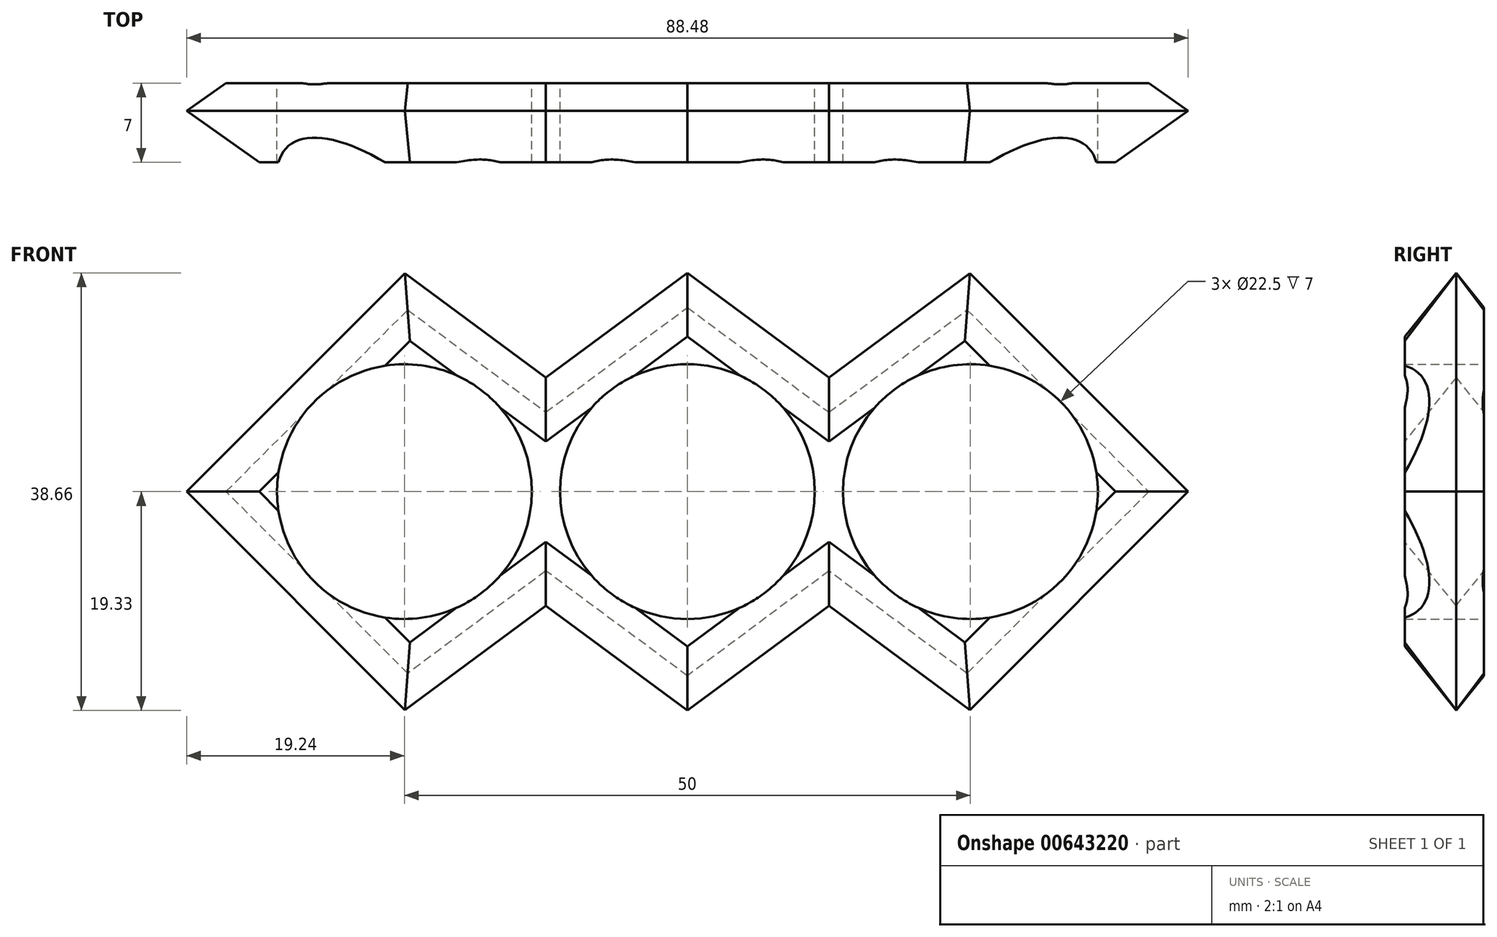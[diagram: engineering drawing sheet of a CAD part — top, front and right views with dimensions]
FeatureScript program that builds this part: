
annotation { "Feature Type Name" : "Feature", "Feature Type Description" : "" }
export const myFeature = defineFeature(function(context is Context, id is Id, definition is map)
    precondition{}
    {
        {
            var Q0;
            Q0=qCreatedBy(makeId("Front.planeOp"),FACE);
            var sketch = newSketch(context, id + "F0", { "sketchPlane" : qUnion([Q0])});
            skCircle(sketch, "E0", {"center": v(0, 0) * mm, "radius": 11.25 * mm});
            skLineSegment(sketch, "E1", {"start": v(0, 0) * mm, "end": v(-25, 0) * mm});
            skLineSegment(sketch, "E2.MirrorCS", {"start": v(0, 0) * mm, "end": v(25, 0) * mm});
            skCircle(sketch, "E3", {"center": v(-25, 0) * mm, "radius": 11.25 * mm});
            skCircle(sketch, "E4", {"center": v(25, 0) * mm, "radius": 11.25 * mm});
            skLineSegment(sketch, "E5", {"start": v(-25, 0) * mm, "end": v(-45, 0) * mm});
            skLineSegment(sketch, "E6.MirrorCS", {"start": v(25, 0) * mm, "end": v(45, 0) * mm});
            skLineSegment(sketch, "E7", {"start": v(-25, 0) * mm, "end": v(-25, 20) * mm});
            skLineSegment(sketch, "E8", {"start": v(-25, 0) * mm, "end": v(-25, -20) * mm});
            skLineSegment(sketch, "E9", {"start": v(-12.5, 0) * mm, "end": v(-12.5, 10.75) * mm});
            skLineSegment(sketch, "E10.MirrorCS", {"start": v(-12.5, 0) * mm, "end": v(-12.5, -10.75) * mm});
            skLineSegment(sketch, "E11", {"start": v(0, 0) * mm, "end": v(0, 20) * mm});
            skLineSegment(sketch, "E12", {"start": v(0, 0) * mm, "end": v(0, -20) * mm});
            skLineSegment(sketch, "E13.MirrorCS", {"start": v(12.5, 0) * mm, "end": v(12.5, 10.75) * mm});
            skLineSegment(sketch, "E14.MirrorCS", {"start": v(12.5, 0) * mm, "end": v(12.5, -10.75) * mm});
            skLineSegment(sketch, "E15", {"start": v(-45, 0) * mm, "end": v(-25, -20) * mm});
            skLineSegment(sketch, "E16", {"start": v(-25, -20) * mm, "end": v(-12.5, -10.75) * mm});
            skLineSegment(sketch, "E17", {"start": v(-12.5, -10.75) * mm, "end": v(0, -20) * mm});
            skLineSegment(sketch, "E18", {"start": v(0, -20) * mm, "end": v(12.5, -10.75) * mm});
            skLineSegment(sketch, "E19", {"start": v(-12.5, 10.75) * mm, "end": v(-25, 20) * mm});
            skLineSegment(sketch, "E20", {"start": v(-25, 20) * mm, "end": v(-45, 0) * mm});
            skLineSegment(sketch, "E21", {"start": v(-12.5, 10.75) * mm, "end": v(0, 20) * mm});
            skLineSegment(sketch, "E22.MirrorCS", {"start": v(12.5, 10.75) * mm, "end": v(0, 20) * mm});
            skLineSegment(sketch, "E23.MirrorCS", {"start": v(12.5, 10.75) * mm, "end": v(25, 20) * mm});
            skLineSegment(sketch, "E24.MirrorCS", {"start": v(25, 20) * mm, "end": v(45, 0) * mm});
            skLineSegment(sketch, "E25.MirrorCS", {"start": v(45, 0) * mm, "end": v(25, -20) * mm});
            skLineSegment(sketch, "E26.MirrorCS", {"start": v(25, -20) * mm, "end": v(12.5, -10.75) * mm});
            skSolve(sketch);
        }
        {
            var Q0;
            {var subQ5=sQuery(id+"F0.wireOp",EDGE,"E20");Q0=makeQuery(id+"F0.imprint","IMPRINT",FACE,{"disambiguationData":[TD([[makeQuery(id+"F0.imprint","IMPRINT",EDGE,{"derivedFrom":subQ5}),1.0]])]});}
            var Q1;
            {var subQ6=sQuery(id+"F0.wireOp",EDGE,"E9");Q1=makeQuery(id+"F0.imprint","IMPRINT",FACE,{"disambiguationData":[TD([[makeQuery(id+"F0.imprint","IMPRINT",EDGE,{"derivedFrom":subQ6}),1.0]])]});}
            var Q2;
            {var subQ0=sQuery(id+"F0.wireOp",EDGE,"E10.MirrorCS");Q2=makeQuery(id+"F0.imprint","IMPRINT",FACE,{"disambiguationData":[TD([[makeQuery(id+"F0.imprint","IMPRINT",EDGE,{"derivedFrom":subQ0}),-1.0]])]});}
            var Q3;
            {var subQ5=sQuery(id+"F0.wireOp",EDGE,"E15");Q3=makeQuery(id+"F0.imprint","IMPRINT",FACE,{"disambiguationData":[TD([[makeQuery(id+"F0.imprint","IMPRINT",EDGE,{"derivedFrom":subQ5}),1.0]])]});}
            var Q4;
            {var subQ4=sQuery(id+"F0.wireOp",EDGE,"E10.MirrorCS");Q4=makeQuery(id+"F0.imprint","IMPRINT",FACE,{"disambiguationData":[TD([[makeQuery(id+"F0.imprint","IMPRINT",EDGE,{"derivedFrom":subQ4}),1.0]])]});}
            var Q5;
            {var subQ4=sQuery(id+"F0.wireOp",EDGE,"E14.MirrorCS");Q5=makeQuery(id+"F0.imprint","IMPRINT",FACE,{"disambiguationData":[TD([[makeQuery(id+"F0.imprint","IMPRINT",EDGE,{"derivedFrom":subQ4}),-1.0]])]});}
            var Q6;
            {var subQ0=sQuery(id+"F0.wireOp",EDGE,"E13.MirrorCS");Q6=makeQuery(id+"F0.imprint","IMPRINT",FACE,{"disambiguationData":[TD([[makeQuery(id+"F0.imprint","IMPRINT",EDGE,{"derivedFrom":subQ0}),1.0]])]});}
            var Q7;
            {var subQ4=sQuery(id+"F0.wireOp",EDGE,"E9");Q7=makeQuery(id+"F0.imprint","IMPRINT",FACE,{"disambiguationData":[TD([[makeQuery(id+"F0.imprint","IMPRINT",EDGE,{"derivedFrom":subQ4}),-1.0]])]});}
            var Q8;
            {var subQ0=sQuery(id+"F0.wireOp",EDGE,"E13.MirrorCS");Q8=makeQuery(id+"F0.imprint","IMPRINT",FACE,{"disambiguationData":[TD([[makeQuery(id+"F0.imprint","IMPRINT",EDGE,{"derivedFrom":subQ0}),-1.0]])]});}
            var Q9;
            {var subQ0=sQuery(id+"F0.wireOp",EDGE,"E14.MirrorCS");Q9=makeQuery(id+"F0.imprint","IMPRINT",FACE,{"disambiguationData":[TD([[makeQuery(id+"F0.imprint","IMPRINT",EDGE,{"derivedFrom":subQ0}),1.0]])]});}
            extrude(context, id + "F1", {"entities" : qUnion([Q0, Q1, Q2, Q3, Q4, Q5, Q6, Q7, Q8, Q9]), "depth" : 7 * mm, "offsetDistance" : 25.4 * mm});
        }
        {
            var Q0;
            Q0=makeQuery(id+"F1.opExtrude","CAP_EDGE",EDGE,{"disambiguationData":[OSD([sQuery(id+"F0.wireOp",EDGE,"E20")])],"isStart":false});
            var Q1;
            Q1=makeQuery(id+"F1.opExtrude","CAP_EDGE",EDGE,{"disambiguationData":[OSD([sQuery(id+"F0.wireOp",EDGE,"E19")])],"isStart":false});
            var Q2;
            Q2=makeQuery(id+"F1.opExtrude","CAP_EDGE",EDGE,{"disambiguationData":[OSD([sQuery(id+"F0.wireOp",EDGE,"E21")])],"isStart":false});
            var Q3;
            Q3=makeQuery(id+"F1.opExtrude","CAP_EDGE",EDGE,{"disambiguationData":[OSD([sQuery(id+"F0.wireOp",EDGE,"E22.MirrorCS")])],"isStart":false});
            var Q4;
            Q4=makeQuery(id+"F1.opExtrude","CAP_EDGE",EDGE,{"disambiguationData":[OSD([sQuery(id+"F0.wireOp",EDGE,"E23.MirrorCS")])],"isStart":false});
            var Q5;
            Q5=makeQuery(id+"F1.opExtrude","CAP_EDGE",EDGE,{"disambiguationData":[OSD([sQuery(id+"F0.wireOp",EDGE,"E24.MirrorCS")])],"isStart":false});
            var Q6;
            Q6=makeQuery(id+"F1.opExtrude","CAP_EDGE",EDGE,{"disambiguationData":[OSD([sQuery(id+"F0.wireOp",EDGE,"E25.MirrorCS")])],"isStart":false});
            var Q7;
            Q7=makeQuery(id+"F1.opExtrude","CAP_EDGE",EDGE,{"disambiguationData":[OSD([sQuery(id+"F0.wireOp",EDGE,"E26.MirrorCS")])],"isStart":false});
            var Q8;
            Q8=makeQuery(id+"F1.opExtrude","CAP_EDGE",EDGE,{"disambiguationData":[OSD([sQuery(id+"F0.wireOp",EDGE,"E18")])],"isStart":false});
            var Q9;
            Q9=makeQuery(id+"F1.opExtrude","CAP_EDGE",EDGE,{"disambiguationData":[OSD([sQuery(id+"F0.wireOp",EDGE,"E17")])],"isStart":false});
            var Q10;
            Q10=makeQuery(id+"F1.opExtrude","CAP_EDGE",EDGE,{"disambiguationData":[OSD([sQuery(id+"F0.wireOp",EDGE,"E16")])],"isStart":false});
            var Q11;
            Q11=makeQuery(id+"F1.opExtrude","CAP_EDGE",EDGE,{"disambiguationData":[OSD([sQuery(id+"F0.wireOp",EDGE,"E15")])],"isStart":false});
            chamfer(context, id + "F2", {"entities" : qUnion([Q0, Q1, Q2, Q3, Q4, Q5, Q6, Q7, Q8, Q9, Q10, Q11]), "width" : 5.08 * mm, "tangentPropagation" : true});
        }
        {
            var Q0;
            Q0=makeQuery(id+"F1.opExtrude","CAP_EDGE",EDGE,{"disambiguationData":[OSD([sQuery(id+"F0.wireOp",EDGE,"E26.MirrorCS")])],"isStart":true});
            var Q1;
            Q1=makeQuery(id+"F1.opExtrude","CAP_EDGE",EDGE,{"disambiguationData":[OSD([sQuery(id+"F0.wireOp",EDGE,"E25.MirrorCS")])],"isStart":true});
            var Q2;
            Q2=makeQuery(id+"F1.opExtrude","CAP_EDGE",EDGE,{"disambiguationData":[OSD([sQuery(id+"F0.wireOp",EDGE,"E18")])],"isStart":true});
            var Q3;
            Q3=makeQuery(id+"F1.opExtrude","CAP_EDGE",EDGE,{"disambiguationData":[OSD([sQuery(id+"F0.wireOp",EDGE,"E17")])],"isStart":true});
            var Q4;
            Q4=makeQuery(id+"F1.opExtrude","CAP_EDGE",EDGE,{"disambiguationData":[OSD([sQuery(id+"F0.wireOp",EDGE,"E16")])],"isStart":true});
            var Q5;
            Q5=makeQuery(id+"F1.opExtrude","CAP_EDGE",EDGE,{"disambiguationData":[OSD([sQuery(id+"F0.wireOp",EDGE,"E15")])],"isStart":true});
            var Q6;
            Q6=makeQuery(id+"F1.opExtrude","CAP_EDGE",EDGE,{"disambiguationData":[OSD([sQuery(id+"F0.wireOp",EDGE,"E20")])],"isStart":true});
            var Q7;
            Q7=makeQuery(id+"F1.opExtrude","CAP_EDGE",EDGE,{"disambiguationData":[OSD([sQuery(id+"F0.wireOp",EDGE,"E19")])],"isStart":true});
            var Q8;
            Q8=makeQuery(id+"F1.opExtrude","CAP_EDGE",EDGE,{"disambiguationData":[OSD([sQuery(id+"F0.wireOp",EDGE,"E21")])],"isStart":true});
            var Q9;
            Q9=makeQuery(id+"F1.opExtrude","CAP_EDGE",EDGE,{"disambiguationData":[OSD([sQuery(id+"F0.wireOp",EDGE,"E22.MirrorCS")])],"isStart":true});
            var Q10;
            Q10=makeQuery(id+"F1.opExtrude","CAP_EDGE",EDGE,{"disambiguationData":[OSD([sQuery(id+"F0.wireOp",EDGE,"E23.MirrorCS")])],"isStart":true});
            var Q11;
            Q11=makeQuery(id+"F1.opExtrude","CAP_EDGE",EDGE,{"disambiguationData":[OSD([sQuery(id+"F0.wireOp",EDGE,"E24.MirrorCS")])],"isStart":true});
            chamfer(context, id + "F3", {"entities" : qUnion([Q0, Q1, Q2, Q3, Q4, Q5, Q6, Q7, Q8, Q9, Q10, Q11]), "width" : 3 * mm, "tangentPropagation" : true});
        }
    });
